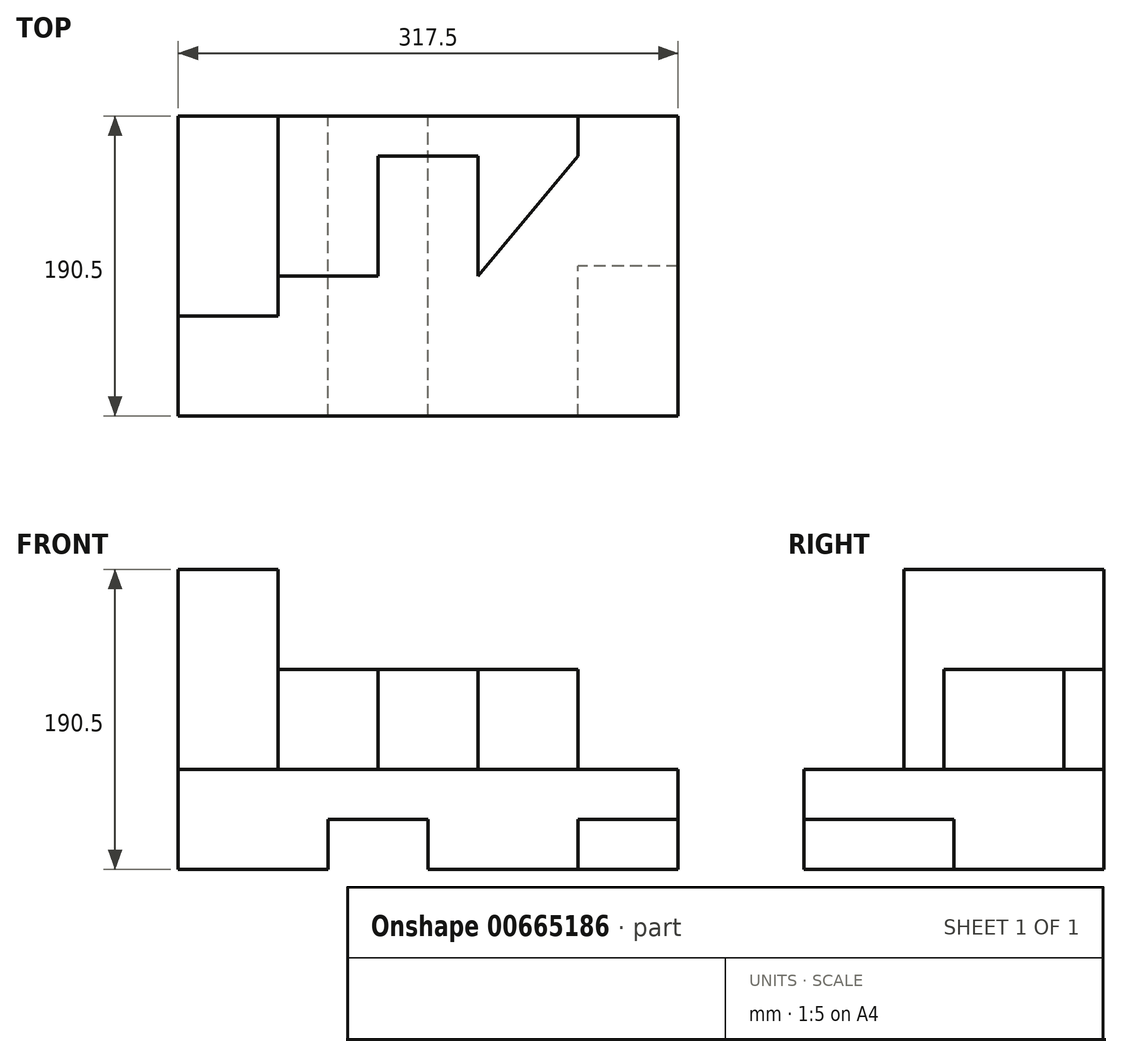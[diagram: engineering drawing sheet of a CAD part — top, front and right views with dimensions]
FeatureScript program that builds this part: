
annotation { "Feature Type Name" : "Feature", "Feature Type Description" : "" }
export const myFeature = defineFeature(function(context is Context, id is Id, definition is map)
    precondition{}
    {
        {
            var Q0;
            Q0=qCreatedBy(makeId("Front.planeOp"),FACE);
            var sketch = newSketch(context, id + "F0", { "sketchPlane" : qUnion([Q0])});
            skLineSegment(sketch, "E0", {"start": v(0, 0) * mm, "end": v(95.25, 0) * mm});
            skLineSegment(sketch, "E1", {"start": v(95.25, 0) * mm, "end": v(95.25, 31.75) * mm});
            skLineSegment(sketch, "E2", {"start": v(95.25, 31.75) * mm, "end": v(158.75, 31.75) * mm});
            skLineSegment(sketch, "E3", {"start": v(158.75, 31.75) * mm, "end": v(158.75, 0) * mm});
            skLineSegment(sketch, "E4", {"start": v(63.5, 127) * mm, "end": v(63.5, 190.5) * mm});
            skLineSegment(sketch, "E5", {"start": v(63.5, 190.5) * mm, "end": v(0, 190.5) * mm});
            skLineSegment(sketch, "E6", {"start": v(0, 190.5) * mm, "end": v(0, 0) * mm});
            skLineSegment(sketch, "E7", {"start": v(63.5, 127) * mm, "end": v(254, 127) * mm});
            skLineSegment(sketch, "E8", {"start": v(254, 127) * mm, "end": v(254, 63.5) * mm});
            skLineSegment(sketch, "E9", {"start": v(254, 63.5) * mm, "end": v(317.5, 63.5) * mm});
            skLineSegment(sketch, "E10", {"start": v(317.5, 63.5) * mm, "end": v(317.5, 0) * mm});
            skLineSegment(sketch, "E11", {"start": v(317.5, 0) * mm, "end": v(158.75, 0) * mm});
            skLineSegment(sketch, "E12", {"start": v(254, 63.5) * mm, "end": v(0, 63.5) * mm});
            skLineSegment(sketch, "E13", {"start": v(63.5, 127) * mm, "end": v(63.5, 63.5) * mm});
            skLineSegment(sketch, "E14", {"start": v(127, 127) * mm, "end": v(127, 63.5) * mm});
            skLineSegment(sketch, "E15", {"start": v(190.5, 127) * mm, "end": v(190.5, 63.5) * mm});
            skLineSegment(sketch, "E16", {"start": v(317.5, 31.75) * mm, "end": v(254, 31.75) * mm});
            skLineSegment(sketch, "E17", {"start": v(254, 31.75) * mm, "end": v(254, 0) * mm});
            skSolve(sketch);
        }
        {
            var Q0;
            {var subQ8=sQuery(id+"F0.wireOp",EDGE,"E0");Q0=makeQuery(id+"F0.imprint","IMPRINT",FACE,{"disambiguationData":[TD([[makeQuery(id+"F0.imprint","IMPRINT",EDGE,{"derivedFrom":subQ8}),1.0]])]});}
            extrude(context, id + "F1", {"entities" : qUnion([Q0]), "depth" : 190.5 * mm, "offsetDistance" : 25.4 * mm});
        }
        {
            var Q0;
            Q0=makeQuery(id+"F0.imprint","IMPRINT",FACE,{"disambiguationData":[TD([[makeQuery(id+"F0.imprint","IMPRINT",EDGE,{"derivedFrom":sQuery(id+"F0.wireOp",EDGE,"E4")}),1.0]])]});
            extrude(context, id + "F2", {"entities" : qUnion([Q0]), "operationType" : NewBodyOperationType.ADD, "depth" : 127 * mm, "offsetDistance" : 25.4 * mm});
        }
        {
            var Q0;
            {var subQ0=sQuery(id+"F0.wireOp",EDGE,"E13");Q0=makeQuery(id+"F0.imprint","IMPRINT",FACE,{"disambiguationData":[TD([[makeQuery(id+"F0.imprint","IMPRINT",EDGE,{"derivedFrom":subQ0}),1.0]])]});}
            var Q1;
            {var subQ0=sQuery(id+"F0.wireOp",EDGE,"E8");Q1=makeQuery(id+"F0.imprint","IMPRINT",FACE,{"disambiguationData":[TD([[makeQuery(id+"F0.imprint","IMPRINT",EDGE,{"derivedFrom":subQ0}),-1.0]])]});}
            extrude(context, id + "F3", {"entities" : qUnion([Q0, Q1]), "operationType" : NewBodyOperationType.ADD, "depth" : 101.6 * mm, "offsetDistance" : 25.4 * mm});
        }
        {
            var Q0;
            {var subQ0=sQuery(id+"F0.wireOp",EDGE,"E14");Q0=makeQuery(id+"F0.imprint","IMPRINT",FACE,{"disambiguationData":[TD([[makeQuery(id+"F0.imprint","IMPRINT",EDGE,{"derivedFrom":subQ0}),1.0]])]});}
            extrude(context, id + "F4", {"entities" : qUnion([Q0]), "operationType" : NewBodyOperationType.ADD, "depth" : 25.4 * mm, "offsetDistance" : 25.4 * mm});
        }
        {
            var Q0;
            {var subQ0=sQuery(id+"F0.wireOp",EDGE,"E7");Q0=makeQuery(id+"F4.boolean.opBoolean","MERGE",FACE,{"derivedFrom":[makeQuery(id+"F3.opExtrude","SWEPT_FACE",FACE,{"disambiguationData":[OSD([subQ0]),TDD([makeQuery(id+"F0.imprint","IMPRINT",EDGE,{"disambiguationData":[TD([[makeQuery(id+"F0.imprint","INTERSECT",VERTEX,{"derivedFrom":[subQ0,sQuery(id+"F0.wireOp",EDGE,"E14")]}),1.0]])],"derivedFrom":subQ0})])]}),makeQuery(id+"F3.opExtrude","SWEPT_FACE",FACE,{"disambiguationData":[OSD([subQ0]),TDD([makeQuery(id+"F0.imprint","IMPRINT",EDGE,{"disambiguationData":[TD([[makeQuery(id+"F0.imprint","INTERSECT",VERTEX,{"derivedFrom":[subQ0,sQuery(id+"F0.wireOp",EDGE,"E8")]}),1.0]])],"derivedFrom":subQ0})])]}),makeQuery(id+"F4.opExtrude","SWEPT_FACE",FACE,{"disambiguationData":[OSD([subQ0])]})]});}
            var sketch = newSketch(context, id + "F5", { "sketchPlane" : qUnion([Q0])});
            skLineSegment(sketch, "E18", {"start": v(190.5, -101.6) * mm, "end": v(254, -25.4) * mm});
            skLineSegment(sketch, "E19", {"start": v(254, -25.4) * mm, "end": v(254, -101.6) * mm});
            skLineSegment(sketch, "E20", {"start": v(254, -101.6) * mm, "end": v(190.5, -101.6) * mm});
            skSolve(sketch);
        }
        {
            var Q0;
            Q0=makeQuery(id+"F5.imprint","IMPRINT",FACE,{"disambiguationData":[TD([[makeQuery(id+"F5.imprint","IMPRINT",EDGE,{"derivedFrom":sQuery(id+"F5.wireOp",EDGE,"E18")}),-1.0]])]});
            extrude(context, id + "F6", {"entities" : qUnion([Q0]), "operationType" : NewBodyOperationType.REMOVE, "oppositeDirection" : true, "depth" : 63.5 * mm, "offsetDistance" : 25.4 * mm});
        }
        {
            var Q0;
            {var subQ3=sQuery(id+"F0.wireOp",EDGE,"E16");Q0=makeQuery(id+"F0.imprint","IMPRINT",FACE,{"disambiguationData":[TD([[makeQuery(id+"F0.imprint","IMPRINT",EDGE,{"derivedFrom":subQ3}),1.0]])]});}
            extrude(context, id + "F7", {"entities" : qUnion([Q0]), "operationType" : NewBodyOperationType.ADD, "depth" : 95.25 * mm, "offsetDistance" : 25.4 * mm});
        }
    });
